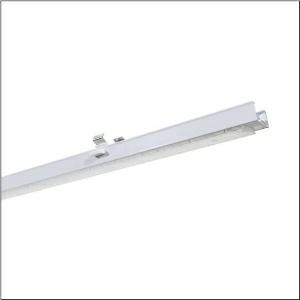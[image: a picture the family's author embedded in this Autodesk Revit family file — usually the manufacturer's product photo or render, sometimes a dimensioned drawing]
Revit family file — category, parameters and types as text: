
# Revit family: trunking_flex_31_51re14mb68b
name_source: partatom
category: Lighting Fixtures
units: mm (PartAtom-declared; Revit-internal decimal feet)

## family parameters
Cut with Voids When Loaded = No
Host = Face
Light Source = No
Part Type = Normal
Room Calculation Point = No
Round Connector Dimension = Use Diameter
Shared = No

## types (1)
- --- (1 x LED, 8000 lm, 50 W, 6500K)
    Apparent Load = 50 VA
    CIE Flux Codes = 72 92 98 99 100
    Color Rendering = 80
    Color Temperature = 6500K
    Default Elevation = 1800 mm
    Description = Trunking Flex 31, luminaire insert, of extruded aluminium section, coated, traffic white (RAL 9016), length: 1.472mm, width: 91mm, height: 53mm, LED rated luminous flux: 8.000lm, light colour: 865, control gear: ON/OFF Multilumen, with system connector: socket, mains connection: 220..240V, AC, 50/60Hz, rated input power: 50W, luminous flux adjustable on luminaire in four steps (4130/5610/6850/8000lm), connected load according to luminous flux setting (25/34/42/50W), primary light control with lens, of plastic, primary optical cover: cover, of PMMA, light emission: direct distribution, primary light characteristic: asymmetric, protection rating (complete): IP20, insulation class (complete): insulation class I (protective earthing), certification: CE, UKCA, impact resistance: IK02, permissible ambient temperature for indoor applications: -20..+40°C, packaging unit: 1 piece
    Height = 58 mm
    Lamp = 1 x LED
    Lamp Light Flux = 8000 lm
    Lamp Power = 50 W
    Lamp count = 1
    Length = 1472 mm
    Luminous efficacy = 160 lm/W
    Manufacturer = Siteco
    ModVariant = No
    Model = 51RE14MB68B
    Mounting Place = Ceiling
    Mounting Type = Pendant
    Number of Poles = 1
    OnlyDefault = Yes
    Power Factor = 1
    Product Name = Trunking Flex 31
    Product group = luminaire insert | ceiling pendant
    ProductGroupID = 902
    Protection Class = Protection class I
    Protection Degree = IP 20
    RLX_Detail_Level = 1
    RLX_Emergency_Light_Flux = 0 lm
    RLX_Emergency_Type = 0
    RLX_Emergency_Type_DB = No
    RlxData = <blob elided: 21109 chars, md5=3f16b5ee>
    Socket = socket
    Standby Power = 0 W
    System Light Flux = 8000 lm
    System Power = 50 W
    Type Comments = factory setting: luminous flux: 100 % | (ON | ON) | 300 mA
    Type Image = l_1266702.jpg
    URL = http://relux.com
    VarID = @adj_079311
    Voltage = 0 V
    Weight = 0.00 kg
    Width = 65 mm

## geometry (parser evidence)
native form markers: Blend x4, Sweep x11
no freeform markers — native parametric forms only
